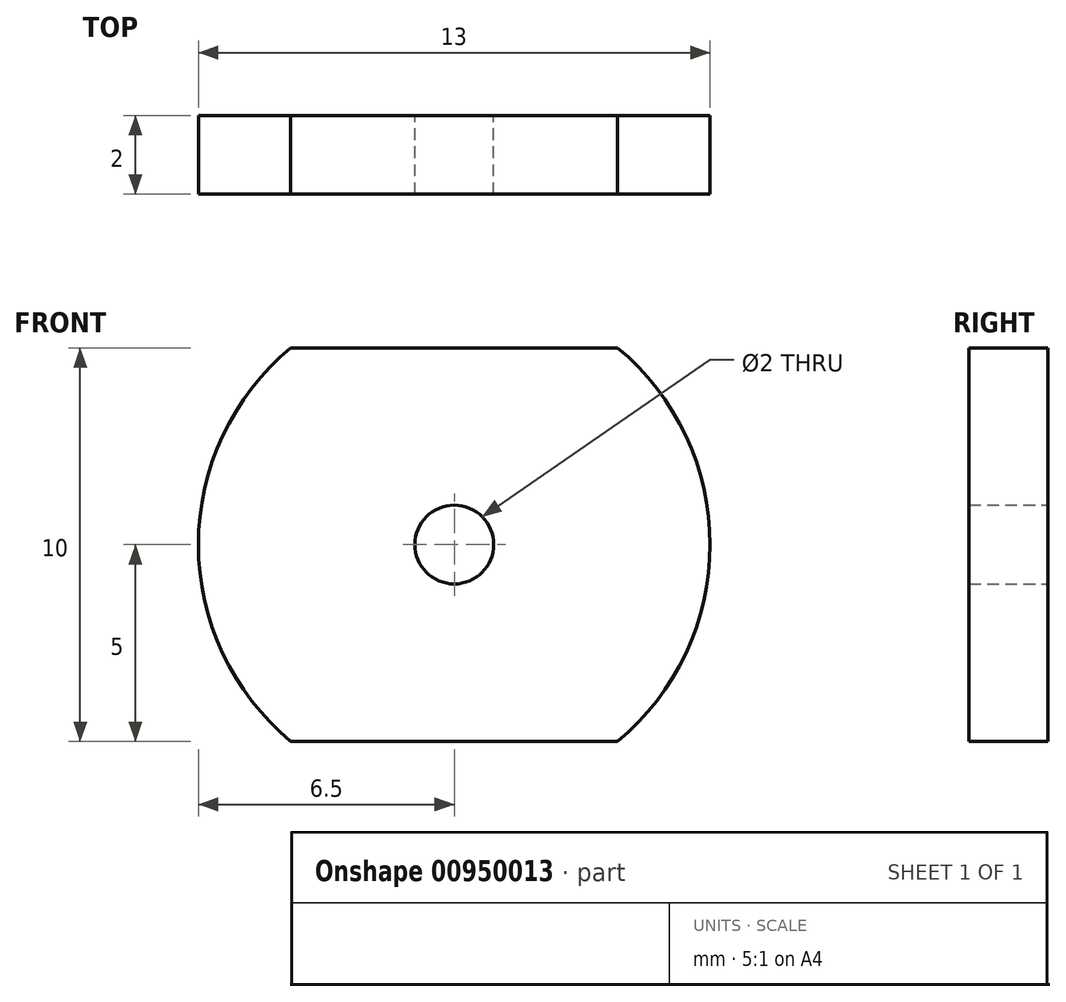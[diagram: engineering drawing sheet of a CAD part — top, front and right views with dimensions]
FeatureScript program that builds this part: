
annotation { "Feature Type Name" : "Feature", "Feature Type Description" : "" }
export const myFeature = defineFeature(function(context is Context, id is Id, definition is map)
    precondition{}
    {
        {
            var Q0;
            Q0=qCreatedBy(makeId("Front.planeOp"),FACE);
            var sketch = newSketch(context, id + "F0", { "sketchPlane" : qUnion([Q0])});
            skArc(sketch, "E0", {"start": v(-4.15, 5) * mm, "mid": v(-6.5, 0) * mm, "end": v(-4.15, -5) * mm});
            skLineSegment(sketch, "E1", {"start": v(-4.15, 5) * mm, "end": v(3.77, 5) * mm});
            skPoint(sketch, "E2.end.orphan", {"position": v(0, 5) * mm});
            skLineSegment(sketch, "E3.MirrorCS", {"start": v(-4.15, -5) * mm, "end": v(3.77, -5) * mm});
            skLineSegment(sketch, "E4", {"start": v(3.77, 5) * mm, "end": v(4.15, 5) * mm});
            skLineSegment(sketch, "E5", {"start": v(3.77, -5) * mm, "end": v(4.15, -5) * mm});
            skArc(sketch, "E6.trimOffspring", {"start": v(4.15, -5) * mm, "mid": v(6.5, 0) * mm, "end": v(4.15, 5) * mm});
            skCircle(sketch, "E7", {"center": v(0, 0) * mm, "radius": 1 * mm});
            skSolve(sketch);
        }
        {
            var Q0;
            Q0=makeQuery(id+"F0.imprint","IMPRINT",FACE,{"disambiguationData":[TD([[makeQuery(id+"F0.imprint","IMPRINT",EDGE,{"derivedFrom":sQuery(id+"F0.wireOp",EDGE,"E0")}),1.0]])]});
            extrude(context, id + "F1", {"entities" : qUnion([Q0]), "depth" : 2 * mm, "offsetDistance" : 25 * mm});
        }
    });
